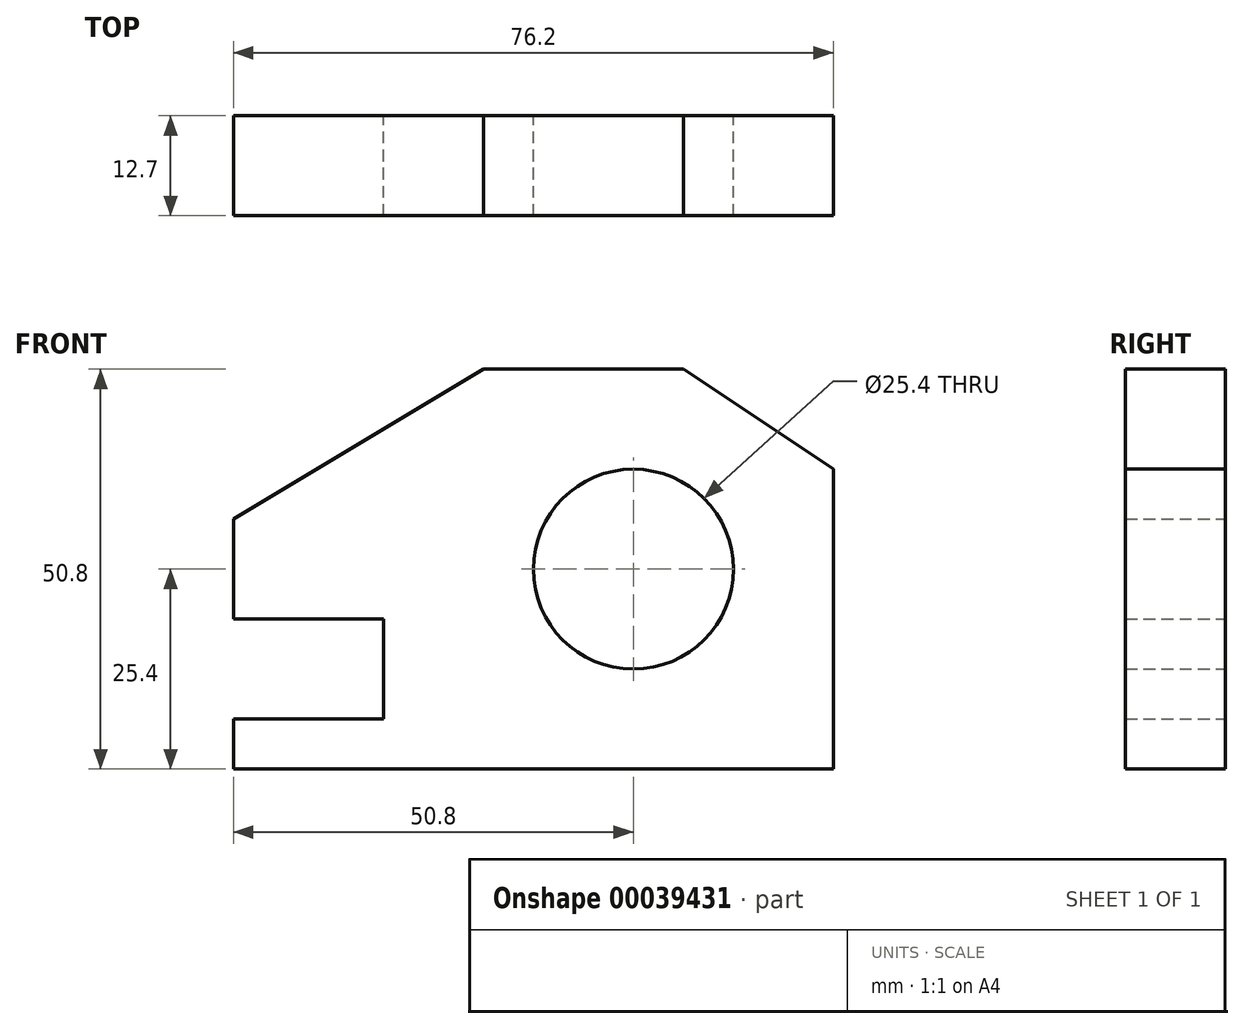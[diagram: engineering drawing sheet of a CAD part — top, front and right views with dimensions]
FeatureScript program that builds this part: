
annotation { "Feature Type Name" : "Feature", "Feature Type Description" : "" }
export const myFeature = defineFeature(function(context is Context, id is Id, definition is map)
    precondition{}
    {
        {
            var Q0;
            Q0=qCreatedBy(makeId("Front.planeOp"),FACE);
            var sketch = newSketch(context, id + "F0", { "sketchPlane" : qUnion([Q0])});
            skCircle(sketch, "E0", {"center": v(0, 0) * mm, "radius": 12.7 * mm});
            skLineSegment(sketch, "E1", {"start": v(25.4, 12.7) * mm, "end": v(25.4, -25.4) * mm});
            skLineSegment(sketch, "E2", {"start": v(25.4, -25.4) * mm, "end": v(-50.8, -25.4) * mm});
            skLineSegment(sketch, "E3", {"start": v(25.4, 12.7) * mm, "end": v(6.35, 25.4) * mm});
            skLineSegment(sketch, "E4", {"start": v(6.35, 25.4) * mm, "end": v(-19.05, 25.4) * mm});
            skLineSegment(sketch, "E5", {"start": v(-50.8, -25.4) * mm, "end": v(-50.8, -19.05) * mm});
            skLineSegment(sketch, "E6", {"start": v(-50.8, -19.05) * mm, "end": v(-31.75, -19.05) * mm});
            skLineSegment(sketch, "E7", {"start": v(-31.75, -6.35) * mm, "end": v(-50.8, -6.35) * mm});
            skLineSegment(sketch, "E8", {"start": v(-50.8, -6.35) * mm, "end": v(-50.8, 6.35) * mm});
            skLineSegment(sketch, "E9", {"start": v(-19.05, 25.4) * mm, "end": v(-50.8, 6.35) * mm});
            skLineSegment(sketch, "E10", {"start": v(-31.75, -6.35) * mm, "end": v(-31.75, -19.05) * mm});
            skSolve(sketch);
        }
        {
            var Q0;
            Q0=makeQuery(id+"F0.imprint","IMPRINT",FACE,{"disambiguationData":[TD([[makeQuery(id+"F0.imprint","IMPRINT",EDGE,{"derivedFrom":sQuery(id+"F0.wireOp",EDGE,"E0")}),-1.0]])]});
            extrude(context, id + "F1", {"entities" : qUnion([Q0]), "depth" : 12.7 * mm});
        }
    });
